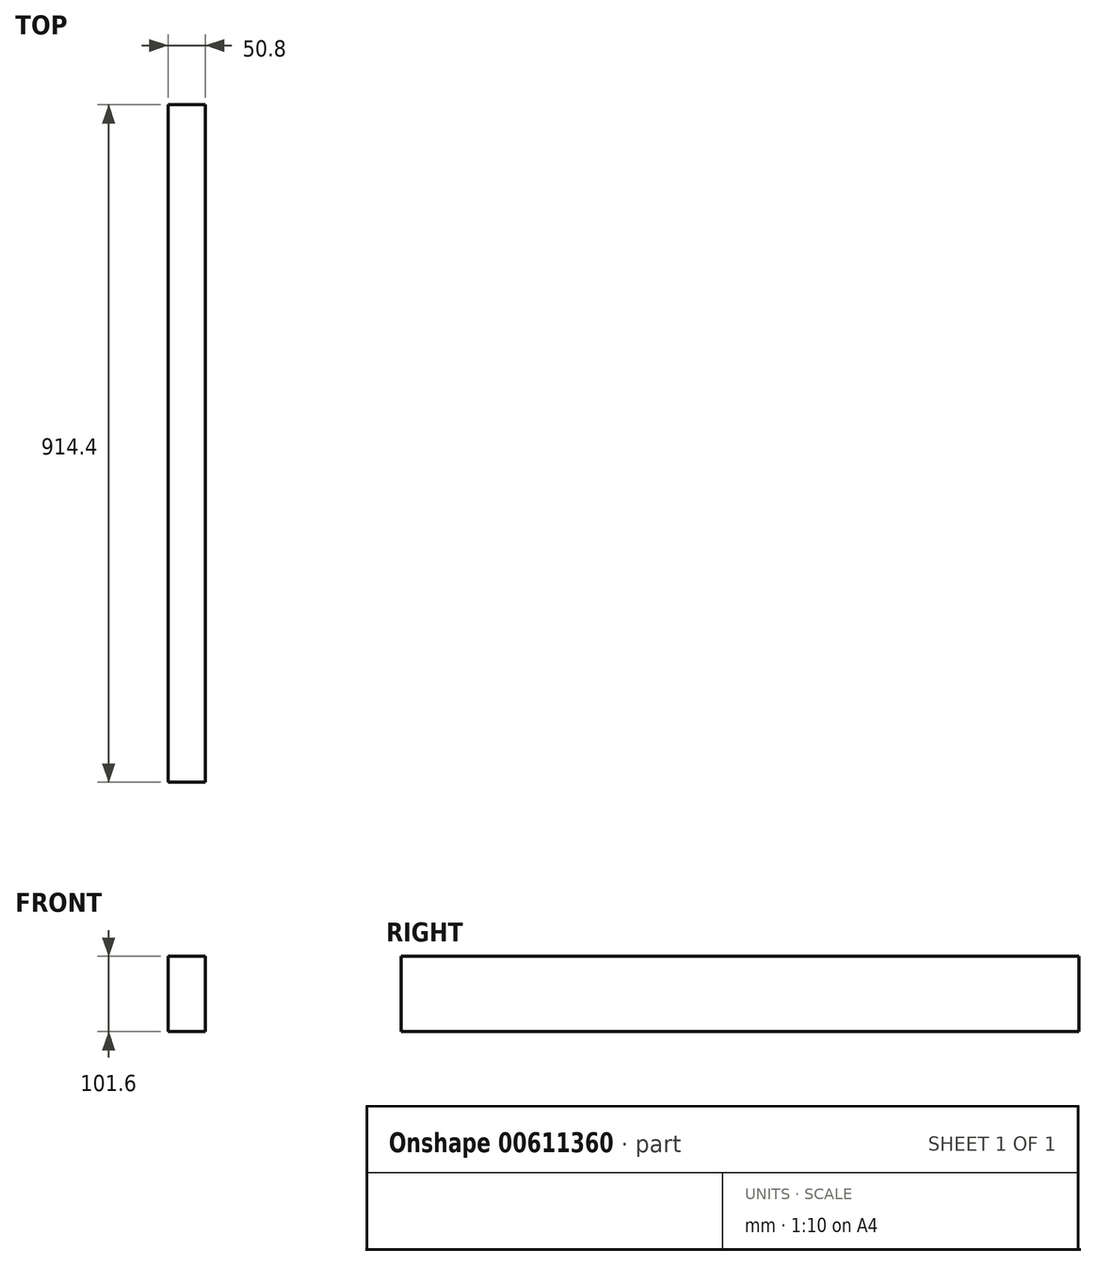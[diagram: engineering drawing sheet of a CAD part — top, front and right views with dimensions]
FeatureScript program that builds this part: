
annotation { "Feature Type Name" : "Feature", "Feature Type Description" : "" }
export const myFeature = defineFeature(function(context is Context, id is Id, definition is map)
    precondition{}
    {
        {
            var Q0;
            Q0=qCreatedBy(makeId("Front.planeOp"),FACE);
            var sketch = newSketch(context, id + "F0", { "sketchPlane" : qUnion([Q0])});
            skLineSegment(sketch, "E0.bottom", {"start": v(-24.18, 50.8) * mm, "end": v(26.62, 50.8) * mm});
            skLineSegment(sketch, "E0.top", {"start": v(-24.18, -50.8) * mm, "end": v(26.62, -50.8) * mm});
            skLineSegment(sketch, "E0.left", {"start": v(-24.18, 50.8) * mm, "end": v(-24.18, -50.8) * mm});
            skLineSegment(sketch, "E0.right", {"start": v(26.62, 50.8) * mm, "end": v(26.62, -50.8) * mm});
            skSolve(sketch);
        }
        {
            var Q0;
            Q0=makeQuery(id+"F0.imprint","IMPRINT",FACE,{"disambiguationData":[TD([[makeQuery(id+"F0.imprint","IMPRINT",EDGE,{"derivedFrom":sQuery(id+"F0.wireOp",EDGE,"E0.bottom")}),-1.0]])]});
            extrude(context, id + "F1", {"entities" : qUnion([Q0]), "depth" : 457.2 * mm, "offsetDistance" : 25.4 * mm, "hasSecondDirection" : true, "secondDirectionOppositeDirection" : true, "secondDirectionDepth" : 457.2 * mm});
        }
    });
